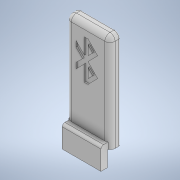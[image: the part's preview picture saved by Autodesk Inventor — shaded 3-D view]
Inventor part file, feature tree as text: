
AUTODESK INVENTOR PART (.ipt)
format: ipt  version: 2020 (Build 240168000, 168)  size: 183,808 bytes
history: native  units: mm
features: fillet x5, extrude x4, sketch x4
ambient origin geometry x8: Origin, YZ Plane, XZ Plane, XY Plane, X Axis, Y Axis, Z Axis, Center Point
bodies: Solid1 (feature_tree)
feature tree (13):
  extrude  "Extrusion1"  Depth=38.0mm
  fillet  "Fillet1"  Radius=4.0mm
  fillet  "Fillet2"  Radius=2.0mm
  extrude  "Extrusion2"  Depth=2.5mm
  fillet  "Fillet3"  Radius=6.0mm
  extrude  "Extrusion3"  Depth=2.5mm
  fillet  "Fillet4"  Radius=16.0mm
  fillet  "Fillet5"  Radius=0.5mm
  extrude  "Extrusion4"  Depth=2.5mm
  sketch  "Sketch1"  dims[d0=17.0mm d1=38.0mm d2=4.0mm d3=0.0mm d4=2.0mm]
  sketch  "Sketch2"  dims[d5=0.5mm d6=2.5mm d7=6.0mm]
  sketch  "Sketch3"  dims[d8=2.5mm d9=2.5mm d10=16.0mm d11=0.0mm d12=0.5mm]
  sketch  "Sketch4"  dims[d13=1.0mm d14=0.0mm d15=2.5mm d16=1.0mm d19=0.5mm d20=0.0mm]
